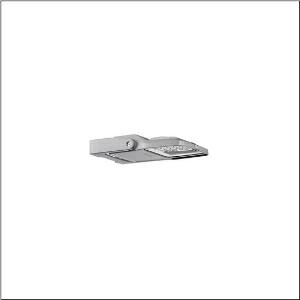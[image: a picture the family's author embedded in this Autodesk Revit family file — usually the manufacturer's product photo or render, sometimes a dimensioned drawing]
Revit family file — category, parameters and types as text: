
# Revit family: floodlight_fl_21_iq_micro___pl64_5xa7762a2e2a_90eb
name_source: partatom
category: Lighting Fixtures
units: mm (PartAtom-declared; Revit-internal decimal feet)

## family parameters
Cut with Voids When Loaded = No
Host = Face
Light Source = No
Part Type = Normal
Room Calculation Point = No
Round Connector Dimension = Use Diameter
Shared = No

## types (1)
- --- (1 x LED, 2870 lm, 23.1 W, 3000K)
    Apparent Load = 23 VA
    CIE Flux Codes = 28 80 98 100 100
    Color Rendering = 70
    Color Temperature = 3000K
    Default Elevation = 1800 mm
    Description = Floodlight FL 21 iQ micro, floodlight, primary light control with lens, of PMMA, primary optical cover: protective disc, of toughened safety glass, transparent, light distribution: PL64, light emission: direct distribution, installation type: surface-mounted, LED, High Power LED, rated luminous flux: 2.870lm, luminous efficacy: 124lm/W, light colour: 730, colour temperature: 3000K, control: Auto-Match, Temp-Guard, Night-Set, Smart-Wire, Desk-Remote (wireless, voltage-free reading and setting of iQ features in the workshop via application-optimized NFC function/RFID function), optimised constant luminous flux control (CLO 2.0), Street-Remote, with terminal, 6-pole, mains connection: 220..240V, AC, 50/60Hz, start of lifetime: 23W, end of service life: 24W, reduction: 11W, luminaire housing, of diecast aluminium, powder-coated, Siteco® metallic grey (DB 702S), corrosivity category C5 mid according to DIN EN ISO 12944, sealing non-destructively replaceable, design bracket, of diecast aluminium, powder-coated, Siteco® metallic grey (DB 702S), protection rating (complete): IP66, insulation class (complete): insulation class II (safety insulation), certification: CE, ENEC, VDE, protection symbol: D, impact resistance: IK07, permissible operating ambient temperature: -40..+40°C, permissible operating ambient temperature for outdoor applications: -40..+50°C, standard: DIN EN 12944, LABS conformity tested according to VDMA 24364:2018-05, packaging unit: 1 piece

Light Distribution: PL64
    Height = 65 mm
    Lamp = 1 x LED
    Lamp Light Flux = 2870 lm
    Lamp Power = 23.1 W
    Lamp count = 1
    Length = 312 mm
    Luminous efficacy = 124 lm/W
    Manufacturer = Siteco
    ModVariant = No
    Model = 5XA7762A2E2A
    Mounting Place = Wall
    Mounting Type = Surface mounted
    Number of Poles = 1
    OnlyDefault = Yes
    Power Factor = 1
    Product Name = Floodlight FL 21 iQ micro | PL64
    Product group = floodlight | wall mounted
    ProductGroupID = 2001
    Protection Class = Protection class II
    Protection Degree = IP 66
    RLX_Detail_Level = 1
    RLX_Emergency_Light_Flux = 0 lm
    RLX_Emergency_Type = 0
    RLX_Emergency_Type_DB = No
    RlxData = <blob elided: 97365 chars, md5=57addcb9>
    Socket = socket
    Standby Power = 0 W
    System Light Flux = 2870 lm
    System Power = 23 W
    Type Comments = factory setting: luminous flux: 100 % | dim-lin: 254 | 455 mA
    Type Image = l_1006878.jpg
    URL = http://relux.com
    VarID = @adj_132051
    Voltage = 0 V
    Weight = 0.00 kg
    Width = 230 mm

## geometry (parser evidence)
native form markers: Blend x4, Sweep x12
no freeform markers — native parametric forms only
